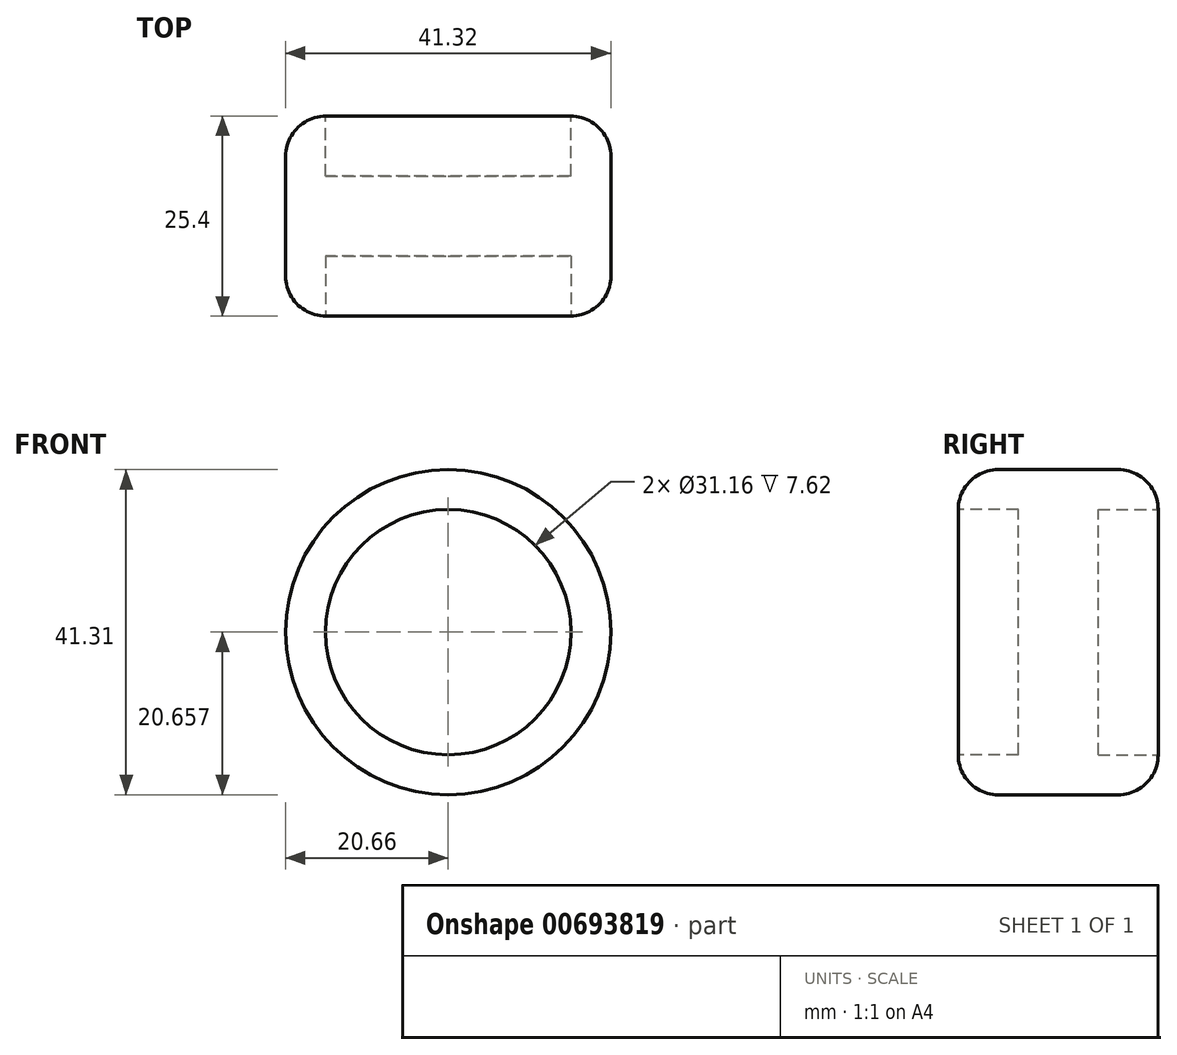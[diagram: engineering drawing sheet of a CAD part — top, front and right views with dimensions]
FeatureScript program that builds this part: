
annotation { "Feature Type Name" : "Feature", "Feature Type Description" : "" }
export const myFeature = defineFeature(function(context is Context, id is Id, definition is map)
    precondition{}
    {
        {
            var Q0;
            Q0=qCreatedBy(makeId("Front.planeOp"),FACE);
            var sketch = newSketch(context, id + "F0", { "sketchPlane" : qUnion([Q0])});
            skLineSegment(sketch, "E0.bottom", {"start": v(-53.15, 13.45) * mm, "end": v(54.73, 13.45) * mm});
            skLineSegment(sketch, "E0.top", {"start": v(-53.15, -12.66) * mm, "end": v(54.73, -12.66) * mm});
            skLineSegment(sketch, "E0.left", {"start": v(-53.15, 13.45) * mm, "end": v(-53.15, -12.66) * mm});
            skLineSegment(sketch, "E0.right", {"start": v(54.73, 13.45) * mm, "end": v(54.73, -12.66) * mm});
            skSolve(sketch);
        }
        {
            var Q0;
            Q0=makeQuery(id+"F0.imprint","IMPRINT",FACE,{"disambiguationData":[TD([[makeQuery(id+"F0.imprint","IMPRINT",EDGE,{"derivedFrom":sQuery(id+"F0.wireOp",EDGE,"E0.bottom")}),-1.0]])]});
            extrude(context, id + "F1", {"entities" : qUnion([Q0]), "depth" : 12.7 * mm, "offsetDistance" : 25.4 * mm});
        }
        {
            var Q0;
            Q0=makeQuery(id+"F1.opExtrude","CAP_FACE",FACE,{"disambiguationData":[OSD([sQuery(id+"F0.wireOp",EDGE,"E0.bottom"),sQuery(id+"F0.wireOp",EDGE,"E0.top"),sQuery(id+"F0.wireOp",EDGE,"E0.left"),sQuery(id+"F0.wireOp",EDGE,"E0.right")])],"isStart":true});
            extrude(context, id + "F2", {"entities" : qUnion([Q0]), "operationType" : NewBodyOperationType.ADD, "depth" : 12.7 * mm, "offsetDistance" : 25.4 * mm});
        }
        {
            var Q0;
            Q0=makeQuery(id+"F1.opExtrude","CAP_FACE",FACE,{"disambiguationData":[OSD([sQuery(id+"F0.wireOp",EDGE,"E0.bottom"),sQuery(id+"F0.wireOp",EDGE,"E0.top"),sQuery(id+"F0.wireOp",EDGE,"E0.left"),sQuery(id+"F0.wireOp",EDGE,"E0.right")])],"isStart":false});
            extrude(context, id + "F3", {"entities" : qUnion([Q0]), "operationType" : NewBodyOperationType.REMOVE, "oppositeDirection" : true, "depth" : 25.4 * mm, "offsetDistance" : 25.4 * mm});
        }
        {
            var Q0;
            Q0=qCreatedBy(makeId("Front.planeOp"),FACE);
            var sketch = newSketch(context, id + "F4", { "sketchPlane" : qUnion([Q0])});
            skCircle(sketch, "E1", {"center": v(0, -189.98) * mm, "radius": 20.66 * mm});
            skSolve(sketch);
        }
        {
            var Q0;
            Q0=makeQuery(id+"F4.imprint","IMPRINT",FACE,{"disambiguationData":[TD([[makeQuery(id+"F4.imprint","IMPRINT",EDGE,{"derivedFrom":sQuery(id+"F4.wireOp",EDGE,"E1")}),1.0]])]});
            extrude(context, id + "F5", {"entities" : qUnion([Q0]), "depth" : 12.7 * mm, "offsetDistance" : 25.4 * mm});
        }
        {
            var Q0;
            Q0=makeQuery(id+"F5.opExtrude","CAP_FACE",FACE,{"disambiguationData":[OSD([sQuery(id+"F4.wireOp",EDGE,"E1")])],"isStart":true});
            extrude(context, id + "F6", {"entities" : qUnion([Q0]), "operationType" : NewBodyOperationType.ADD, "depth" : 12.7 * mm, "offsetDistance" : 25.4 * mm});
        }
        {
            var Q0;
            Q0=makeQuery(id+"F5.opExtrude","CAP_EDGE",EDGE,{"disambiguationData":[OSD([sQuery(id+"F4.wireOp",EDGE,"E1")])],"isStart":false});
            var Q1;
            Q1=makeQuery(id+"F6.opExtrude","CAP_EDGE",EDGE,{"disambiguationData":[OSD([sQuery(id+"F4.wireOp",EDGE,"E1")])],"isStart":false});
            fillet(context, id + "F7", {"entities" : qUnion([Q0, Q1]), "radius" : 5.08 * mm, "tangentPropagation" : true, "allowEdgeOverflow" : false});
        }
        {
            var Q0;
            Q0=makeQuery(id+"F5.opExtrude","CAP_FACE",FACE,{"disambiguationData":[OSD([sQuery(id+"F4.wireOp",EDGE,"E1")])],"isStart":false});
            extrude(context, id + "F8", {"entities" : qUnion([Q0]), "operationType" : NewBodyOperationType.REMOVE, "oppositeDirection" : true, "depth" : 7.62 * mm, "offsetDistance" : 25.4 * mm});
        }
        {
            var Q0;
            Q0=makeQuery(id+"F6.opExtrude","CAP_FACE",FACE,{"disambiguationData":[OSD([sQuery(id+"F4.wireOp",EDGE,"E1")])],"isStart":false});
            extrude(context, id + "F9", {"entities" : qUnion([Q0]), "operationType" : NewBodyOperationType.REMOVE, "oppositeDirection" : true, "depth" : 7.62 * mm, "offsetDistance" : 25.4 * mm});
        }
    });
